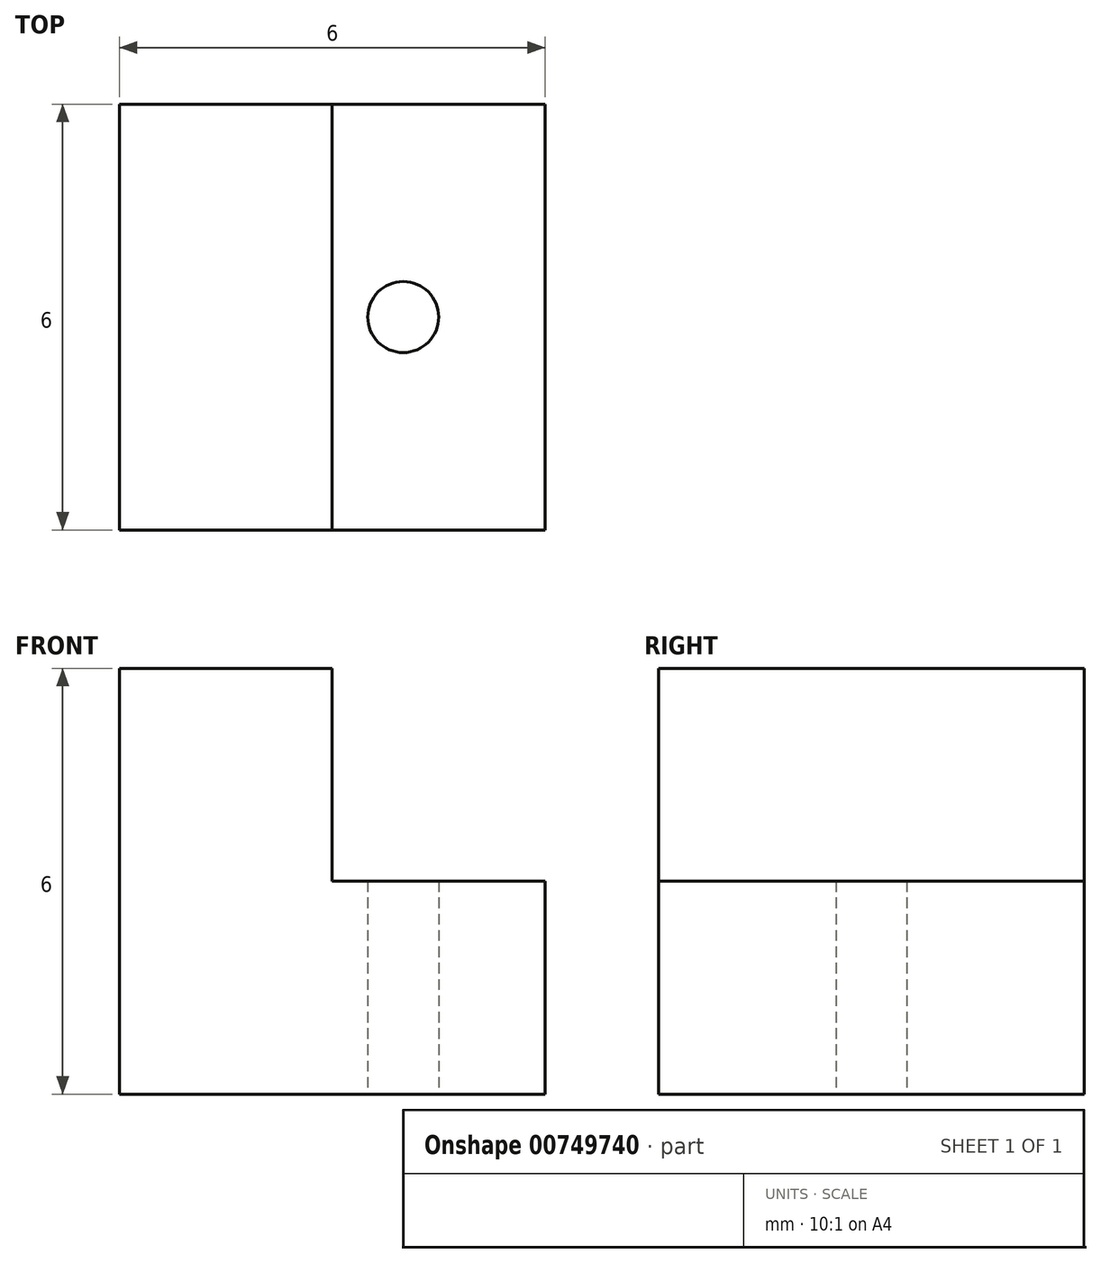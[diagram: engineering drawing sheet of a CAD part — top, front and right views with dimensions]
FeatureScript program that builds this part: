
annotation { "Feature Type Name" : "Feature", "Feature Type Description" : "" }
export const myFeature = defineFeature(function(context is Context, id is Id, definition is map)
    precondition{}
    {
        {
            var Q0;
            Q0=qCreatedBy(makeId("Top.planeOp"),FACE);
            var sketch = newSketch(context, id + "F0", { "sketchPlane" : qUnion([Q0])});
            skLineSegment(sketch, "E0.bottom", {"start": v(0, 0) * mm, "end": v(6, 0) * mm});
            skLineSegment(sketch, "E0.top", {"start": v(0, 6) * mm, "end": v(6, 6) * mm});
            skLineSegment(sketch, "E0.left", {"start": v(0, 0) * mm, "end": v(0, 6) * mm});
            skLineSegment(sketch, "E0.right", {"start": v(6, 0) * mm, "end": v(6, 6) * mm});
            skCircle(sketch, "E1", {"center": v(4, 3) * mm, "radius": 0.5 * mm});
            skLineSegment(sketch, "E2.bottom", {"start": v(6, 6) * mm, "end": v(4, 6) * mm});
            skLineSegment(sketch, "E2.top", {"start": v(8, 0) * mm, "end": v(6, 0) * mm});
            skLineSegment(sketch, "E2.left", {"start": v(6, 6) * mm, "end": v(6, 0) * mm});
            skSolve(sketch);
        }
        {
            var Q0;
            Q0=makeQuery(id+"F0.imprint","IMPRINT",FACE,{"disambiguationData":[TD([[makeQuery(id+"F0.imprint","IMPRINT",EDGE,{"derivedFrom":sQuery(id+"F0.wireOp",EDGE,"E0.bottom")}),1.0]])]});
            extrude(context, id + "F1", {"entities" : qUnion([Q0]), "depth" : 3 * mm, "offsetDistance" : 25 * mm});
        }
        {
            var Q0;
            Q0=qCreatedBy(makeId("Top.planeOp"),FACE);
            var sketch = newSketch(context, id + "F2", { "sketchPlane" : qUnion([Q0])});
            skLineSegment(sketch, "E3.bottom", {"start": v(0, 0) * mm, "end": v(3, 0) * mm});
            skLineSegment(sketch, "E3.top", {"start": v(0, 6) * mm, "end": v(3, 6) * mm});
            skLineSegment(sketch, "E3.left", {"start": v(0, 0) * mm, "end": v(0, 6) * mm});
            skLineSegment(sketch, "E3.right", {"start": v(3, 0) * mm, "end": v(3, 6) * mm});
            skSolve(sketch);
        }
        {
            var Q0;
            Q0 = qSketchRegion(id + "F2", true);
            extrude(context, id + "F3", {"entities" : qUnion([Q0]), "operationType" : NewBodyOperationType.ADD, "depth" : 6 * mm, "offsetDistance" : 25 * mm});
        }
    });
